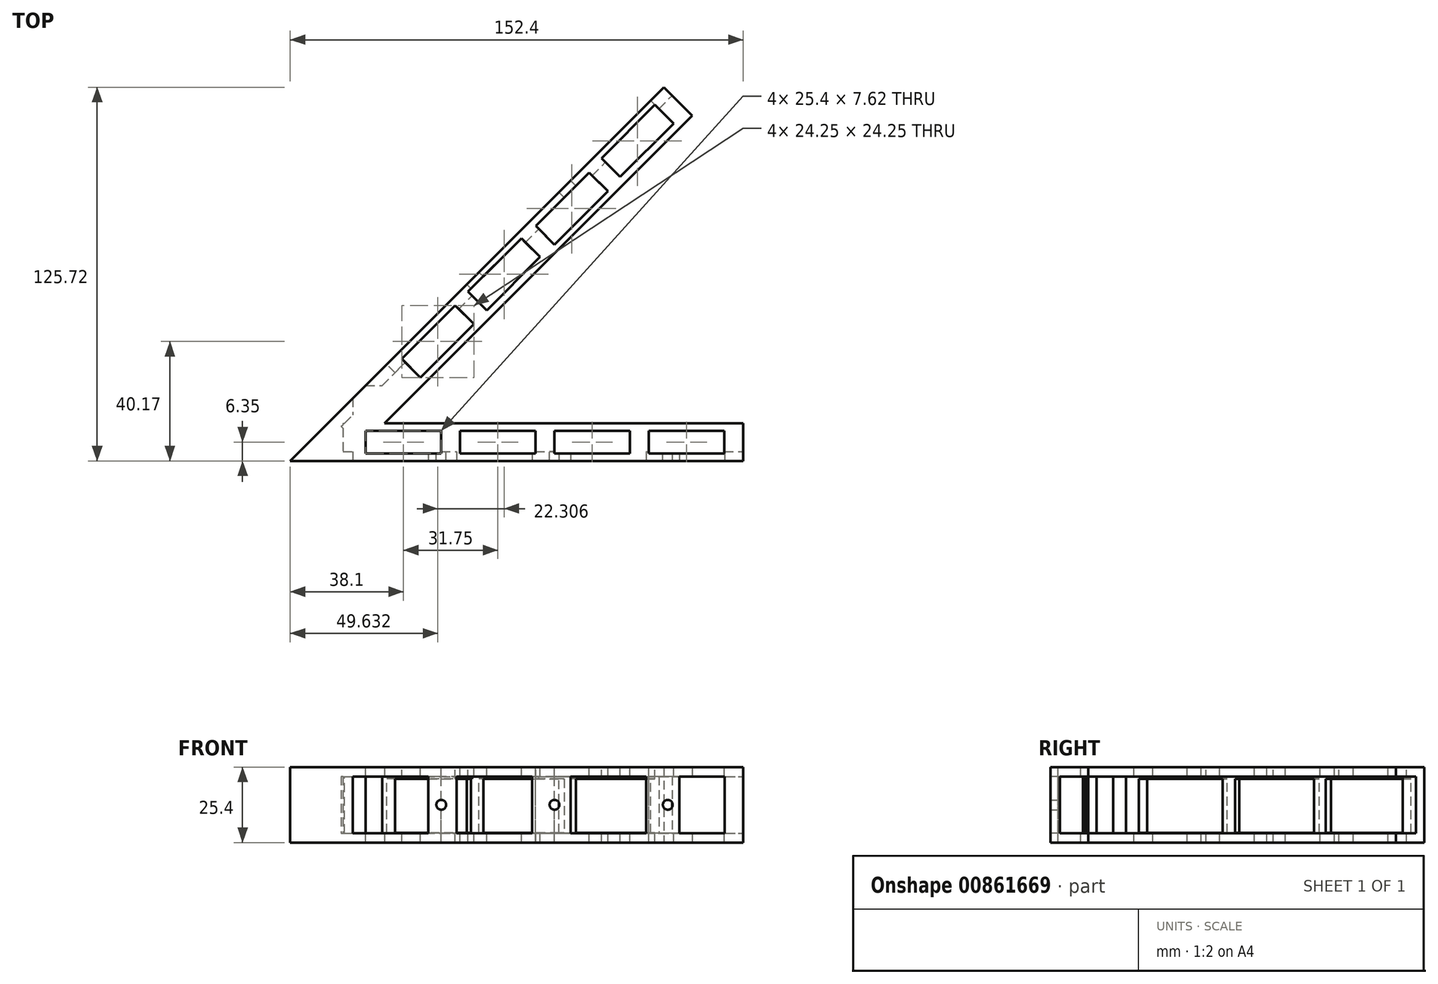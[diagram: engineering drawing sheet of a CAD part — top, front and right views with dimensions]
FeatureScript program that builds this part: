
annotation { "Feature Type Name" : "Feature", "Feature Type Description" : "" }
export const myFeature = defineFeature(function(context is Context, id is Id, definition is map)
    precondition{}
    {
        {
            var Q0;
            Q0=qCreatedBy(makeId("Top.planeOp"),FACE);
            var sketch = newSketch(context, id + "F0", { "sketchPlane" : qUnion([Q0])});
            skLineSegment(sketch, "E0", {"start": v(0, 0) * mm, "end": v(125.72, 125.72) * mm});
            skLineSegment(sketch, "E1", {"start": v(0, 0) * mm, "end": v(152.4, 0) * mm});
            skLineSegment(sketch, "E2", {"start": v(152.4, 0) * mm, "end": v(152.4, 12.7) * mm});
            skLineSegment(sketch, "E3", {"start": v(152.4, 12.7) * mm, "end": v(31.75, 12.7) * mm});
            skLineSegment(sketch, "E4", {"start": v(31.75, 12.7) * mm, "end": v(135.25, 116.2) * mm});
            skLineSegment(sketch, "E5", {"start": v(125.72, 125.72) * mm, "end": v(135.25, 116.2) * mm});
            skSolve(sketch);
        }
        {
            var Q0;
            Q0=makeQuery(id+"F0.imprint","IMPRINT",FACE,{"disambiguationData":[TD([[makeQuery(id+"F0.imprint","IMPRINT",EDGE,{"derivedFrom":sQuery(id+"F0.wireOp",EDGE,"E0")}),-1.0]])]});
            extrude(context, id + "F1", {"entities" : qUnion([Q0]), "depth" : 25.4 * mm, "offsetDistance" : 25.4 * mm});
        }
        {
            var Q0;
            Q0=makeQuery(id+"F1.opExtrude","SWEPT_FACE",FACE,{"disambiguationData":[OSD([sQuery(id+"F0.wireOp",EDGE,"E2")])]});
            var sketch = newSketch(context, id + "F2", { "sketchPlane" : qUnion([Q0])});
            skLineSegment(sketch, "E6.bottom", {"start": v(12.7, 3.18) * mm, "end": v(3.18, 3.18) * mm});
            skLineSegment(sketch, "E6.top", {"start": v(12.7, 22.23) * mm, "end": v(3.17, 22.23) * mm});
            skLineSegment(sketch, "E6.left", {"start": v(12.7, 3.18) * mm, "end": v(12.7, 22.23) * mm});
            skLineSegment(sketch, "E6.right", {"start": v(3.18, 3.18) * mm, "end": v(3.17, 22.23) * mm});
            skSolve(sketch);
        }
        {
            var Q0;
            Q0=makeQuery(id+"F2.imprint","IMPRINT",FACE,{"disambiguationData":[TD([[makeQuery(id+"F2.imprint","IMPRINT",EDGE,{"derivedFrom":sQuery(id+"F2.wireOp",EDGE,"E6.bottom")}),-1.0]])]});
            extrude(context, id + "F3", {"entities" : qUnion([Q0]), "operationType" : NewBodyOperationType.REMOVE, "oppositeDirection" : true, "depth" : 134.62 * mm, "offsetDistance" : 25.4 * mm});
        }
        {
            var Q0;
            Q0=makeQuery(id+"F1.opExtrude","SWEPT_FACE",FACE,{"disambiguationData":[OSD([sQuery(id+"F0.wireOp",EDGE,"E5")])]});
            var sketch = newSketch(context, id + "F4", { "sketchPlane" : qUnion([Q0])});
            skLineSegment(sketch, "E7.bottom", {"start": v(-13.47, 22.23) * mm, "end": v(-3.95, 22.23) * mm});
            skLineSegment(sketch, "E7.top", {"start": v(-13.47, 3.18) * mm, "end": v(-3.95, 3.18) * mm});
            skLineSegment(sketch, "E7.left", {"start": v(-13.47, 22.23) * mm, "end": v(-13.47, 3.18) * mm});
            skLineSegment(sketch, "E7.right", {"start": v(-3.95, 22.23) * mm, "end": v(-3.95, 3.18) * mm});
            skSolve(sketch);
        }
        {
            var Q0;
            Q0=makeQuery(id+"F4.imprint","IMPRINT",FACE,{"disambiguationData":[TD([[makeQuery(id+"F4.imprint","IMPRINT",EDGE,{"derivedFrom":sQuery(id+"F4.wireOp",EDGE,"E7.bottom")}),-1.0]])]});
            extrude(context, id + "F5", {"entities" : qUnion([Q0]), "operationType" : NewBodyOperationType.REMOVE, "oppositeDirection" : true, "depth" : 157.48 * mm, "offsetDistance" : 25.4 * mm});
        }
        {
            var Q0;
            Q0=makeQuery(id+"F3.boolean.opBoolean","COPY",FACE,{"derivedFrom":makeQuery(id+"F3.opExtrude","SWEPT_FACE",FACE,{"disambiguationData":[OSD([sQuery(id+"F2.wireOp",EDGE,"E6.right")])]})});
            var sketch = newSketch(context, id + "F6", { "sketchPlane" : qUnion([Q0])});
            skCircle(sketch, "E8", {"center": v(-127, 12.7) * mm, "radius": 1.65 * mm});
            skCircle(sketch, "E9", {"center": v(-88.9, 12.7) * mm, "radius": 1.65 * mm});
            skCircle(sketch, "E10", {"center": v(-50.8, 12.7) * mm, "radius": 1.65 * mm});
            skSolve(sketch);
        }
        {
            var Q0;
            Q0=makeQuery(id+"F6.imprint","IMPRINT",FACE,{"disambiguationData":[TD([[makeQuery(id+"F6.imprint","IMPRINT",EDGE,{"derivedFrom":sQuery(id+"F6.wireOp",EDGE,"E9")}),1.0]])]});
            var Q1;
            Q1=makeQuery(id+"F6.imprint","IMPRINT",FACE,{"disambiguationData":[TD([[makeQuery(id+"F6.imprint","IMPRINT",EDGE,{"derivedFrom":sQuery(id+"F6.wireOp",EDGE,"E10")}),1.0]])]});
            var Q2;
            Q2=makeQuery(id+"F6.imprint","IMPRINT",FACE,{"disambiguationData":[TD([[makeQuery(id+"F6.imprint","IMPRINT",EDGE,{"derivedFrom":sQuery(id+"F6.wireOp",EDGE,"E8")}),1.0]])]});
            extrude(context, id + "F7", {"entities" : qUnion([Q0, Q1, Q2]), "operationType" : NewBodyOperationType.REMOVE, "oppositeDirection" : true, "depth" : 25.4 * mm, "offsetDistance" : 25.4 * mm});
        }
        {
            var Q0;
            Q0=makeQuery(id+"F1.opExtrude","CAP_FACE",FACE,{"disambiguationData":[OSD([sQuery(id+"F0.wireOp",EDGE,"E0"),sQuery(id+"F0.wireOp",EDGE,"E1"),sQuery(id+"F0.wireOp",EDGE,"E2"),sQuery(id+"F0.wireOp",EDGE,"E3"),sQuery(id+"F0.wireOp",EDGE,"E4"),sQuery(id+"F0.wireOp",EDGE,"E5")])],"isStart":false});
            var sketch = newSketch(context, id + "F8", { "sketchPlane" : qUnion([Q0])});
            skLineSegment(sketch, "E11.bottom", {"start": v(146.05, 10.16) * mm, "end": v(120.65, 10.16) * mm});
            skLineSegment(sketch, "E11.top", {"start": v(146.05, 2.54) * mm, "end": v(120.65, 2.54) * mm});
            skLineSegment(sketch, "E11.left", {"start": v(146.05, 10.16) * mm, "end": v(146.05, 2.54) * mm});
            skLineSegment(sketch, "E11.right", {"start": v(120.65, 10.16) * mm, "end": v(120.65, 2.54) * mm});
            skLineSegment(sketch, "E12.bottom", {"start": v(114.3, 10.16) * mm, "end": v(88.9, 10.16) * mm});
            skLineSegment(sketch, "E12.top", {"start": v(114.3, 2.54) * mm, "end": v(88.9, 2.54) * mm});
            skLineSegment(sketch, "E12.left", {"start": v(114.3, 10.16) * mm, "end": v(114.3, 2.54) * mm});
            skLineSegment(sketch, "E12.right", {"start": v(88.9, 10.16) * mm, "end": v(88.9, 2.54) * mm});
            skLineSegment(sketch, "E13.bottom", {"start": v(82.55, 10.16) * mm, "end": v(57.15, 10.16) * mm});
            skLineSegment(sketch, "E13.top", {"start": v(82.55, 2.54) * mm, "end": v(57.15, 2.54) * mm});
            skLineSegment(sketch, "E13.left", {"start": v(82.55, 10.16) * mm, "end": v(82.55, 2.54) * mm});
            skLineSegment(sketch, "E13.right", {"start": v(57.15, 10.16) * mm, "end": v(57.15, 2.54) * mm});
            skLineSegment(sketch, "E14.bottom", {"start": v(50.8, 10.16) * mm, "end": v(25.4, 10.16) * mm});
            skLineSegment(sketch, "E14.top", {"start": v(50.8, 2.54) * mm, "end": v(25.4, 2.54) * mm});
            skLineSegment(sketch, "E14.left", {"start": v(50.8, 10.16) * mm, "end": v(50.8, 2.54) * mm});
            skLineSegment(sketch, "E14.right", {"start": v(25.4, 10.16) * mm, "end": v(25.4, 2.54) * mm});
            skLineSegment(sketch, "E15", {"start": v(122.68, 119.8) * mm, "end": v(128.96, 113.5) * mm});
            skLineSegment(sketch, "E16", {"start": v(128.96, 113.5) * mm, "end": v(111, 95.54) * mm});
            skLineSegment(sketch, "E17", {"start": v(111, 95.54) * mm, "end": v(104.72, 101.83) * mm});
            skLineSegment(sketch, "E18", {"start": v(104.72, 101.83) * mm, "end": v(122.68, 119.8) * mm});
            skLineSegment(sketch, "E19", {"start": v(100.58, 96.99) * mm, "end": v(106.87, 90.7) * mm});
            skLineSegment(sketch, "E20", {"start": v(106.87, 90.7) * mm, "end": v(88.9, 72.74) * mm});
            skLineSegment(sketch, "E21", {"start": v(88.9, 72.74) * mm, "end": v(82.62, 79.03) * mm});
            skLineSegment(sketch, "E22", {"start": v(82.62, 79.03) * mm, "end": v(100.58, 96.99) * mm});
            skLineSegment(sketch, "E23", {"start": v(77.77, 74.89) * mm, "end": v(84.06, 68.6) * mm});
            skLineSegment(sketch, "E24", {"start": v(84.06, 68.6) * mm, "end": v(66.1, 50.64) * mm});
            skLineSegment(sketch, "E25", {"start": v(66.1, 50.64) * mm, "end": v(59.81, 56.93) * mm});
            skLineSegment(sketch, "E26", {"start": v(59.81, 56.93) * mm, "end": v(77.77, 74.89) * mm});
            skLineSegment(sketch, "E27", {"start": v(55.47, 52.3) * mm, "end": v(61.76, 46) * mm});
            skLineSegment(sketch, "E28", {"start": v(61.76, 46) * mm, "end": v(43.8, 28.05) * mm});
            skLineSegment(sketch, "E29", {"start": v(43.8, 28.05) * mm, "end": v(37.5, 34.33) * mm});
            skLineSegment(sketch, "E30", {"start": v(37.5, 34.33) * mm, "end": v(55.47, 52.3) * mm});
            skSolve(sketch);
        }
        {
            var Q0;
            Q0=makeQuery(id+"F8.imprint","IMPRINT",FACE,{"disambiguationData":[TD([[makeQuery(id+"F8.imprint","IMPRINT",EDGE,{"derivedFrom":sQuery(id+"F8.wireOp",EDGE,"E14.bottom")}),1.0]])]});
            var Q1;
            Q1=makeQuery(id+"F8.imprint","IMPRINT",FACE,{"disambiguationData":[TD([[makeQuery(id+"F8.imprint","IMPRINT",EDGE,{"derivedFrom":sQuery(id+"F8.wireOp",EDGE,"E13.bottom")}),1.0]])]});
            var Q2;
            Q2=makeQuery(id+"F8.imprint","IMPRINT",FACE,{"disambiguationData":[TD([[makeQuery(id+"F8.imprint","IMPRINT",EDGE,{"derivedFrom":sQuery(id+"F8.wireOp",EDGE,"E12.bottom")}),1.0]])]});
            var Q3;
            Q3=makeQuery(id+"F8.imprint","IMPRINT",FACE,{"disambiguationData":[TD([[makeQuery(id+"F8.imprint","IMPRINT",EDGE,{"derivedFrom":sQuery(id+"F8.wireOp",EDGE,"E11.bottom")}),1.0]])]});
            var Q4;
            Q4=makeQuery(id+"F8.imprint","IMPRINT",FACE,{"disambiguationData":[TD([[makeQuery(id+"F8.imprint","IMPRINT",EDGE,{"derivedFrom":sQuery(id+"F8.wireOp",EDGE,"E15")}),-1.0]])]});
            var Q5;
            Q5=makeQuery(id+"F8.imprint","IMPRINT",FACE,{"disambiguationData":[TD([[makeQuery(id+"F8.imprint","IMPRINT",EDGE,{"derivedFrom":sQuery(id+"F8.wireOp",EDGE,"E19")}),-1.0]])]});
            var Q6;
            Q6=makeQuery(id+"F8.imprint","IMPRINT",FACE,{"disambiguationData":[TD([[makeQuery(id+"F8.imprint","IMPRINT",EDGE,{"derivedFrom":sQuery(id+"F8.wireOp",EDGE,"E23")}),-1.0]])]});
            var Q7;
            Q7=makeQuery(id+"F8.imprint","IMPRINT",FACE,{"disambiguationData":[TD([[makeQuery(id+"F8.imprint","IMPRINT",EDGE,{"derivedFrom":sQuery(id+"F8.wireOp",EDGE,"E27")}),-1.0]])]});
            extrude(context, id + "F9", {"entities" : qUnion([Q0, Q1, Q2, Q3, Q4, Q5, Q6, Q7]), "operationType" : NewBodyOperationType.REMOVE, "oppositeDirection" : true, "depth" : 101.6 * mm, "offsetDistance" : 25.4 * mm});
        }
        {
            var Q0;
            Q0=makeQuery(id+"F1.opExtrude","SWEPT_FACE",FACE,{"disambiguationData":[OSD([sQuery(id+"F0.wireOp",EDGE,"E1")])]});
            var sketch = newSketch(context, id + "F10", { "sketchPlane" : qUnion([Q0])});
            skLineSegment(sketch, "E31.bottom", {"start": v(21.05, 22.23) * mm, "end": v(46.45, 22.23) * mm});
            skLineSegment(sketch, "E31.top", {"start": v(21.05, 3.18) * mm, "end": v(46.45, 3.18) * mm});
            skLineSegment(sketch, "E31.left", {"start": v(21.05, 22.23) * mm, "end": v(21.05, 3.18) * mm});
            skLineSegment(sketch, "E31.right", {"start": v(46.45, 22.23) * mm, "end": v(46.45, 3.18) * mm});
            skLineSegment(sketch, "E32.bottom", {"start": v(56.01, 22.22) * mm, "end": v(81.41, 22.22) * mm});
            skLineSegment(sketch, "E32.top", {"start": v(56.01, 3.17) * mm, "end": v(81.41, 3.17) * mm});
            skLineSegment(sketch, "E32.left", {"start": v(56.01, 22.22) * mm, "end": v(56.01, 3.17) * mm});
            skLineSegment(sketch, "E32.right", {"start": v(81.41, 22.22) * mm, "end": v(81.41, 3.17) * mm});
            skLineSegment(sketch, "E33.bottom", {"start": v(94.3, 22.22) * mm, "end": v(119.7, 22.22) * mm});
            skLineSegment(sketch, "E33.top", {"start": v(94.3, 3.17) * mm, "end": v(119.7, 3.17) * mm});
            skLineSegment(sketch, "E33.left", {"start": v(94.3, 22.22) * mm, "end": v(94.3, 3.17) * mm});
            skLineSegment(sketch, "E33.right", {"start": v(119.7, 22.22) * mm, "end": v(119.7, 3.17) * mm});
            skLineSegment(sketch, "E34.bottom", {"start": v(130.84, 22.23) * mm, "end": v(146.08, 22.23) * mm});
            skLineSegment(sketch, "E34.top", {"start": v(130.84, 3.18) * mm, "end": v(146.08, 3.18) * mm});
            skLineSegment(sketch, "E34.left", {"start": v(130.84, 22.23) * mm, "end": v(130.84, 3.18) * mm});
            skLineSegment(sketch, "E34.right", {"start": v(146.08, 22.23) * mm, "end": v(146.08, 3.18) * mm});
            skSolve(sketch);
        }
        {
            var Q0;
            Q0=makeQuery(id+"F10.imprint","IMPRINT",FACE,{"disambiguationData":[TD([[makeQuery(id+"F10.imprint","IMPRINT",EDGE,{"derivedFrom":sQuery(id+"F10.wireOp",EDGE,"E34.bottom")}),-1.0]])]});
            var Q1;
            Q1=makeQuery(id+"F10.imprint","IMPRINT",FACE,{"disambiguationData":[TD([[makeQuery(id+"F10.imprint","IMPRINT",EDGE,{"derivedFrom":sQuery(id+"F10.wireOp",EDGE,"E33.bottom")}),-1.0]])]});
            var Q2;
            Q2=makeQuery(id+"F10.imprint","IMPRINT",FACE,{"disambiguationData":[TD([[makeQuery(id+"F10.imprint","IMPRINT",EDGE,{"derivedFrom":sQuery(id+"F10.wireOp",EDGE,"E32.bottom")}),-1.0]])]});
            var Q3;
            Q3=makeQuery(id+"F10.imprint","IMPRINT",FACE,{"disambiguationData":[TD([[makeQuery(id+"F10.imprint","IMPRINT",EDGE,{"derivedFrom":sQuery(id+"F10.wireOp",EDGE,"E31.bottom")}),-1.0]])]});
            extrude(context, id + "F11", {"entities" : qUnion([Q0, Q1, Q2, Q3]), "operationType" : NewBodyOperationType.REMOVE, "oppositeDirection" : true, "depth" : 25.4 * mm, "offsetDistance" : 25.4 * mm});
        }
        {
            var Q0;
            Q0=makeQuery(id+"F1.opExtrude","SWEPT_FACE",FACE,{"disambiguationData":[OSD([sQuery(id+"F0.wireOp",EDGE,"E0")])]});
            var sketch = newSketch(context, id + "F12", { "sketchPlane" : qUnion([Q0])});
            skLineSegment(sketch, "E35.bottom", {"start": v(-171.45, 3.26) * mm, "end": v(-133.35, 3.26) * mm});
            skLineSegment(sketch, "E35.top", {"start": v(-171.45, 21.42) * mm, "end": v(-133.35, 21.42) * mm});
            skLineSegment(sketch, "E35.left", {"start": v(-171.45, 3.26) * mm, "end": v(-171.45, 21.42) * mm});
            skLineSegment(sketch, "E35.right", {"start": v(-133.35, 3.26) * mm, "end": v(-133.35, 21.42) * mm});
            skLineSegment(sketch, "E36.bottom", {"start": v(-127.87, 3.26) * mm, "end": v(-89.77, 3.26) * mm});
            skLineSegment(sketch, "E36.top", {"start": v(-127.87, 21.42) * mm, "end": v(-89.77, 21.42) * mm});
            skLineSegment(sketch, "E36.left", {"start": v(-127.87, 3.26) * mm, "end": v(-127.87, 21.42) * mm});
            skLineSegment(sketch, "E36.right", {"start": v(-89.77, 3.26) * mm, "end": v(-89.77, 21.42) * mm});
            skLineSegment(sketch, "E37.bottom", {"start": v(-83.96, 3.26) * mm, "end": v(-45.86, 3.26) * mm});
            skLineSegment(sketch, "E37.top", {"start": v(-83.96, 21.42) * mm, "end": v(-45.86, 21.42) * mm});
            skLineSegment(sketch, "E37.left", {"start": v(-83.96, 3.26) * mm, "end": v(-83.96, 21.42) * mm});
            skLineSegment(sketch, "E37.right", {"start": v(-45.86, 3.26) * mm, "end": v(-45.86, 21.42) * mm});
            skSolve(sketch);
        }
        {
            var Q0;
            Q0=makeQuery(id+"F12.imprint","IMPRINT",FACE,{"disambiguationData":[TD([[makeQuery(id+"F12.imprint","IMPRINT",EDGE,{"derivedFrom":sQuery(id+"F12.wireOp",EDGE,"E36.bottom")}),1.0]])]});
            var Q1;
            Q1=makeQuery(id+"F12.imprint","IMPRINT",FACE,{"disambiguationData":[TD([[makeQuery(id+"F12.imprint","IMPRINT",EDGE,{"derivedFrom":sQuery(id+"F12.wireOp",EDGE,"E35.bottom")}),1.0]])]});
            var Q2;
            Q2=makeQuery(id+"F12.imprint","IMPRINT",FACE,{"disambiguationData":[TD([[makeQuery(id+"F12.imprint","IMPRINT",EDGE,{"derivedFrom":sQuery(id+"F12.wireOp",EDGE,"E37.bottom")}),1.0]])]});
            extrude(context, id + "F13", {"entities" : qUnion([Q0, Q1, Q2]), "operationType" : NewBodyOperationType.REMOVE, "oppositeDirection" : true, "depth" : 25.4 * mm, "offsetDistance" : 25.4 * mm});
        }
    });
